# Revit family: CADS_Vent-Axia_IntegraPlus
name_source: partatom
category: Mechanical Equipment
revit_build: Autodesk Revit 2015 (Build: 20160512_1515(x64)
units: mm (PartAtom-declared; Revit-internal decimal feet)

## types (1)
- Integra Plus EC
    Apparent Load = 690 VA
    AssetType = Fixed
    C = 100 mm  [stored 0.328084 ft]
    Category = Pr_60_60_36:Heat recovery distribution equipment
    Color = Black
    D = 64 mm  [stored 0.209974 ft]
    Default Elevation = 1219 mm
    Description = Integra Plus EC
    DurationUnit = year
    E = 125 mm  [stored 0.410105 ft]
    ExpectedLife = 20
    H = 305 mm  [stored 1.00066 ft]
    I = 83 mm
    IfcExportAs = IfcAirToAirHeatRecoveryType
    IfcExportType = USERDEFINED
    Manufacturer = Vent-Axia Limited
    Material = ABS Plastic
    Model = Integra Plus EC
    ModelNumber = 437666EC
    ModelReference = Integra Plus EC
    Name = MVHR Unit
    NominalHeight = 305 mm  [stored 1.00066 ft]
    NominalLength = 580 mm  [stored 1.90289 ft]
    NominalWidth = 580 mm  [stored 1.90289 ft]
    NumberOfPoles = 1
    RatedCurrent = 3 A
    RatedVoltage = 230 V
    Shape = Rectangular
    Size = 580mm x 580mm x 305mm 
570mm x 849mm x 200mm
    SpigotDiameter = 150 mm
    Version = 1.0
    WarrantyDurationLabor = 2
    WarrantyDurationMotors = 5
    WarrantyDurationParts = 2
    WarrantyDurationUnit = year

note: [stored X ft] marks values corroborated as IEEE doubles in the binary element streams (Revit-internal decimal feet)

## geometry (parser evidence)
native form markers: Sweep x16
no freeform markers — native parametric forms only
